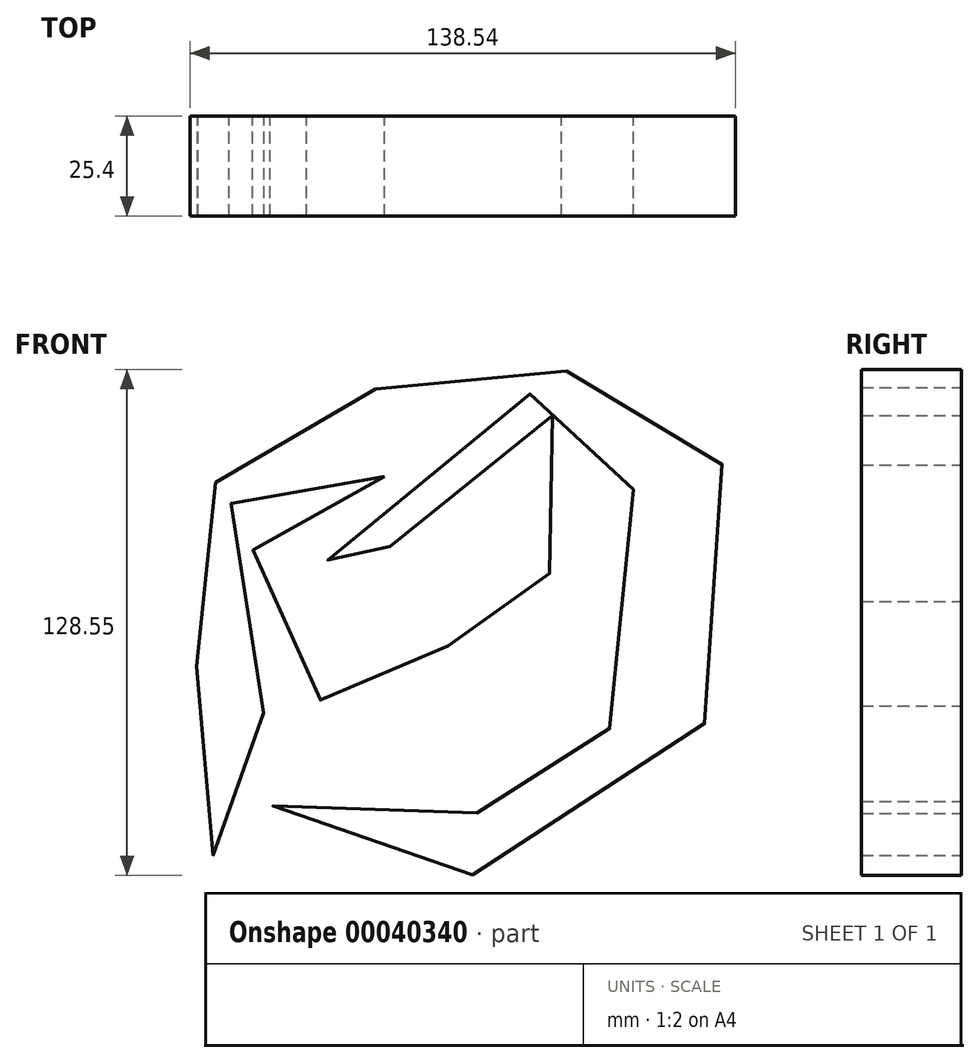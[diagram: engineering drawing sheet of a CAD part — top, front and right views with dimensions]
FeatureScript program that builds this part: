
annotation { "Feature Type Name" : "Feature", "Feature Type Description" : "" }
export const myFeature = defineFeature(function(context is Context, id is Id, definition is map)
    precondition{}
    {
        {
            var Q0;
            Q0=qCreatedBy(makeId("Front.planeOp"),FACE);
            var sketch = newSketch(context, id + "F0", { "sketchPlane" : qUnion([Q0])});
            skFitSpline(sketch, "E0", {"points": [v(-23.92, 45.87) * mm, v(-55.04, 34.02) * mm, v(-48.08, 6.39) * mm, v(-37.86, -12.43) * mm, v(-16.72, 0) * mm, v(13.93, 8.24) * mm, v(18.58, 31) * mm, v(19.5, 60.97) * mm, v(-14.86, 34.72) * mm, v(-43.66, 14.52) * mm, v(-3.48, 58.64) * mm, v(34.37, 63.52) * mm, v(36.46, 7.78) * mm, v(24.62, -34.95) * mm, v(-23.92, -37.74) * mm, v(-52.95, -39.37) * mm, v(24.39, -52.6) * mm, v(65.26, 26.6) * mm, v(47.84, 66.08) * mm, v(-2.32, 72.35) * mm, v(-37.16, 63.98) * mm, v(-69.9, 39.6) * mm, v(-71.53, -3.83) * mm, v(-68.28, -50.05) * mm, v(-59, -41.69) * mm, v(-57.37, 6.85) * mm, v(-58.3, 45.17) * mm, v(-23.92, 45.87) * mm]});
            skSolve(sketch);
        }
        {
            var Q0;
            Q0=makeQuery(id+"F0.imprint","IMPRINT",FACE,{"disambiguationData":[TD([[makeQuery(id+"F0.imprint","IMPRINT",EDGE,{"derivedFrom":sQuery(id+"F0.wireOp",EDGE,"E0")}),1.0]])]});
            extrude(context, id + "F1", {"entities" : qUnion([Q0]), "depth" : 25.4 * mm});
        }
    });
